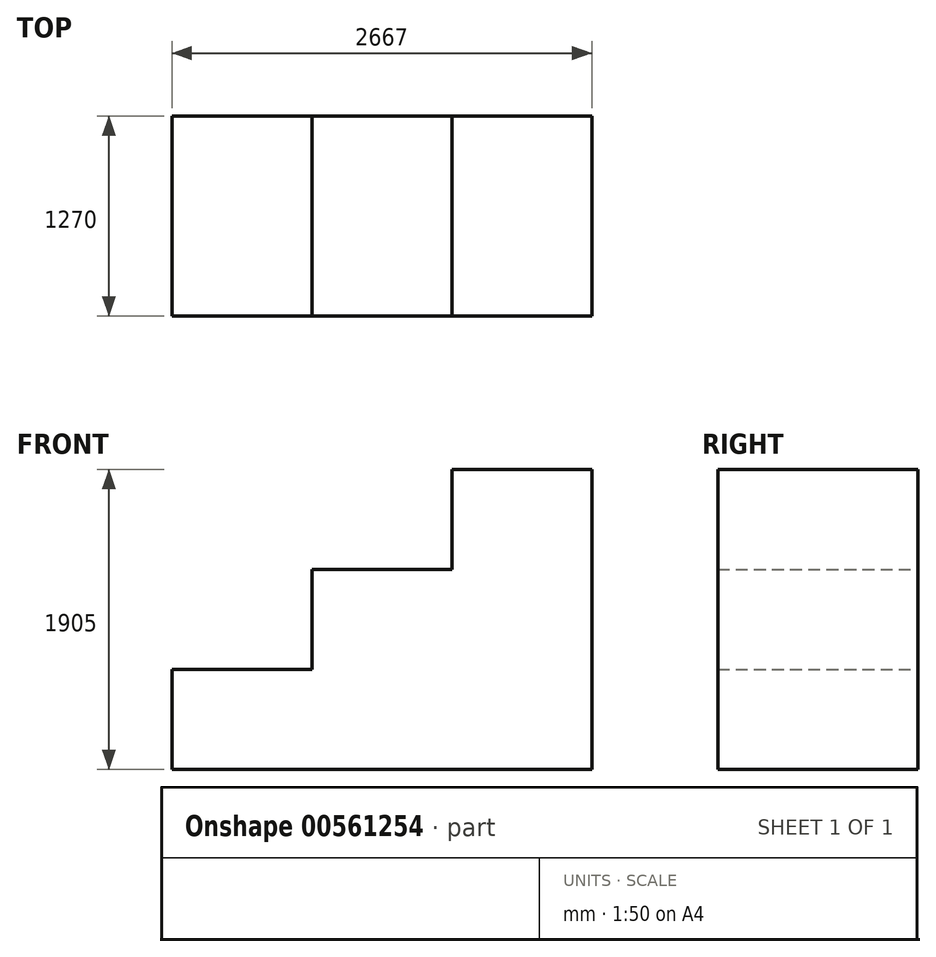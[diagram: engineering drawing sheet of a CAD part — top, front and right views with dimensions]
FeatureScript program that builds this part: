
annotation { "Feature Type Name" : "Feature", "Feature Type Description" : "" }
export const myFeature = defineFeature(function(context is Context, id is Id, definition is map)
    precondition{}
    {
        {
            var Q0;
            Q0=qCreatedBy(makeId("Front.planeOp"),FACE);
            var sketch = newSketch(context, id + "F0", { "sketchPlane" : qUnion([Q0])});
            skLineSegment(sketch, "E0.top", {"start": v(1333.5, -952.5) * mm, "end": v(-1333.5, -952.5) * mm});
            skLineSegment(sketch, "E0.left", {"start": v(1333.5, 952.5) * mm, "end": v(1333.5, -952.5) * mm});
            skPoint(sketch, "E0.middle", {"position": v(0, 0) * mm});
            skLineSegment(sketch, "E1", {"start": v(1333.5, 952.5) * mm, "end": v(444.5, 952.5) * mm});
            skLineSegment(sketch, "E2", {"start": v(444.5, 952.5) * mm, "end": v(444.5, 317.5) * mm});
            skLineSegment(sketch, "E3", {"start": v(444.5, 317.5) * mm, "end": v(-444.5, 317.5) * mm});
            skLineSegment(sketch, "E4", {"start": v(-444.5, 317.5) * mm, "end": v(-444.5, -317.5) * mm});
            skLineSegment(sketch, "E5", {"start": v(-444.5, -317.5) * mm, "end": v(-1333.5, -317.5) * mm});
            skLineSegment(sketch, "E6", {"start": v(-1333.5, -952.5) * mm, "end": v(-1333.5, -317.5) * mm});
            skSolve(sketch);
        }
        {
            var Q0;
            Q0=makeQuery(id+"F0.imprint","IMPRINT",FACE,{"disambiguationData":[TD([[makeQuery(id+"F0.imprint","IMPRINT",EDGE,{"derivedFrom":sQuery(id+"F0.wireOp",EDGE,"E0.top")}),-1.0]])]});
            extrude(context, id + "F1", {"entities" : qUnion([Q0]), "depth" : 1270 * mm, "offsetDistance" : 25.4 * mm});
        }
    });
